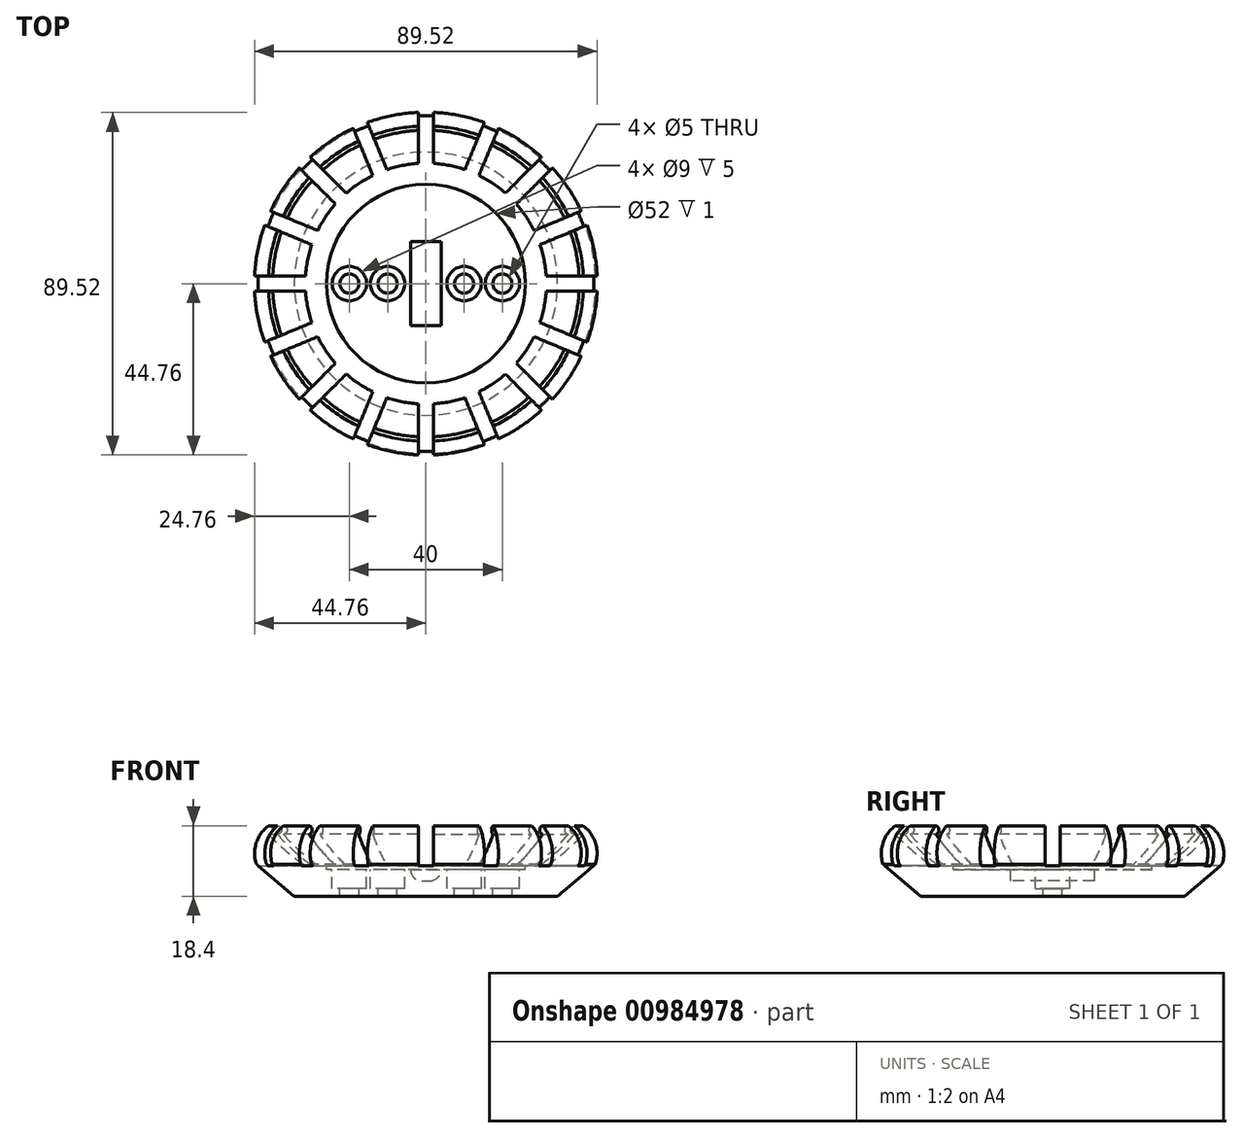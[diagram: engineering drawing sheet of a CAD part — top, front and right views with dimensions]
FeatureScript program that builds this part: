
annotation { "Feature Type Name" : "Feature", "Feature Type Description" : "" }
export const myFeature = defineFeature(function(context is Context, id is Id, definition is map)
    precondition{}
    {
        {
            var Q0;
            Q0=qCreatedBy(makeId("Front.planeOp"),FACE);
            var sketch = newSketch(context, id + "F0", { "sketchPlane" : qUnion([Q0])});
            skLineSegment(sketch, "E0", {"start": v(0, 0) * mm, "end": v(-31.5, 0) * mm});
            skArc(sketch, "E1", {"start": v(-41.2, 8.2) * mm, "mid": v(-36.58, 3.83) * mm, "end": v(-31.5, 0) * mm});
            skPoint(sketch, "E2.start.orphan", {"position": v(0, 8.2) * mm});
            skArc(sketch, "E3", {"start": v(-41.2, 8.2) * mm, "mid": v(-40.1, 9.3) * mm, "end": v(-41.2, 10.4) * mm});
            skLineSegment(sketch, "E4.trimOffspring", {"start": v(-41.2, 10.4) * mm, "end": v(-41.2, 14.25) * mm});
            skLineSegment(sketch, "E5", {"start": v(0, -8) * mm, "end": v(-34.43, -8) * mm});
            skLineSegment(sketch, "E6", {"start": v(-34.43, -8) * mm, "end": v(-44.37, 0.4) * mm});
            skArc(sketch, "E7", {"start": v(-41.2, 10.4) * mm, "mid": v(-44.4, 5.9) * mm, "end": v(-44.37, 0.4) * mm});
            skLineSegment(sketch, "E8.MirrorCS", {"start": v(0, 0) * mm, "end": v(31.5, 0) * mm});
            skArc(sketch, "E9.MirrorCS", {"start": v(41.2, 10.4) * mm, "mid": v(44.4, 5.9) * mm, "end": v(44.37, 0.4) * mm});
            skLineSegment(sketch, "E10.MirrorCS", {"start": v(41.2, 10.4) * mm, "end": v(41.2, 14.25) * mm});
            skLineSegment(sketch, "E11.MirrorCS", {"start": v(34.43, -8) * mm, "end": v(44.37, 0.4) * mm});
            skLineSegment(sketch, "E12.MirrorCS", {"start": v(0, -8) * mm, "end": v(34.43, -8) * mm});
            skArc(sketch, "E13.MirrorCS", {"start": v(41.2, 8.2) * mm, "mid": v(40.1, 9.3) * mm, "end": v(41.2, 10.4) * mm});
            skArc(sketch, "E14.MirrorCS", {"start": v(41.2, 8.2) * mm, "mid": v(36.58, 3.83) * mm, "end": v(31.5, 0) * mm});
            skLineSegment(sketch, "E15", {"start": v(0, 60.69) * mm, "end": v(0, -49.12) * mm});
            skSolve(sketch);
        }
        {
            var Q0;
            {var subQ1=sQuery(id+"F0.wireOp",EDGE,"E8.MirrorCS");Q0=makeQuery(id+"F0.imprint","IMPRINT",FACE,{"disambiguationData":[TD([[makeQuery(id+"F0.imprint","IMPRINT",EDGE,{"derivedFrom":subQ1}),-1.0]])]});}
            var Q1;
            Q1=sQuery(id+"F0.wireOp",EDGE,"E15");
            revolve(context, id + "F1", {"surfaceOperationType" : NewSurfaceOperationType.NEW, "entities" : qUnion([Q0]), "axis" : qUnion([Q1]), "revolveType" : RevolveType.FULL});
        }
        {
            var Q0;
            Q0=makeQuery(id+"F1.opRevolve","SWEPT_FACE",FACE,{"disambiguationData":[OSD([sQuery(id+"F0.wireOp",EDGE,"E8.MirrorCS")])]});
            var sketch = newSketch(context, id + "F2", { "sketchPlane" : qUnion([Q0])});
            skCircle(sketch, "E16", {"center": v(0, 0) * mm, "radius": 26 * mm});
            skSolve(sketch);
        }
        {
            var Q0;
            Q0 = qSketchRegion(id + "F2", true);
            extrude(context, id + "F3", {"entities" : qUnion([Q0]), "operationType" : NewBodyOperationType.REMOVE, "oppositeDirection" : true, "depth" : 1 * mm, "offsetDistance" : 25 * mm});
        }
        {
            var Q0;
            Q0=makeQuery(id+"F1.opRevolve","SWEPT_FACE",FACE,{"disambiguationData":[OSD([sQuery(id+"F0.wireOp",EDGE,"E8.MirrorCS")])]});
            var sketch = newSketch(context, id + "F4", { "sketchPlane" : qUnion([Q0])});
            skLineSegment(sketch, "E17.bottom", {"start": v(-2, 51.5) * mm, "end": v(2, 51.5) * mm});
            skLineSegment(sketch, "E17.top", {"start": v(-2, -48.5) * mm, "end": v(2, -48.5) * mm});
            skLineSegment(sketch, "E17.left", {"start": v(-2, 51.5) * mm, "end": v(-2, 4.83) * mm});
            skLineSegment(sketch, "E17.right", {"start": v(2, 51.5) * mm, "end": v(2, 4.83) * mm});
            skLineSegment(sketch, "E18.bottom", {"start": v(-48.8, 2) * mm, "end": v(-4.83, 2) * mm});
            skLineSegment(sketch, "E18.top", {"start": v(-48.8, -2) * mm, "end": v(-4.83, -2) * mm});
            skLineSegment(sketch, "E18.left", {"start": v(-48.8, 2) * mm, "end": v(-48.8, -2) * mm});
            skLineSegment(sketch, "E18.right", {"start": v(51.2, 2) * mm, "end": v(51.2, -2) * mm});
            skLineSegment(sketch, "E19", {"start": v(-36.98, 39.81) * mm, "end": v(-2, 4.83) * mm});
            skLineSegment(sketch, "E20", {"start": v(38.72, -35.9) * mm, "end": v(35.9, -38.72) * mm});
            skLineSegment(sketch, "E21", {"start": v(35.9, -38.72) * mm, "end": v(2, -4.83) * mm});
            skLineSegment(sketch, "E22", {"start": v(-39.72, 36.89) * mm, "end": v(-36.98, 39.81) * mm});
            skLineSegment(sketch, "E23", {"start": v(44.09, 41.26) * mm, "end": v(4.83, 2) * mm});
            skLineSegment(sketch, "E24", {"start": v(-37.99, -40.82) * mm, "end": v(-40.82, -37.99) * mm});
            skLineSegment(sketch, "E25", {"start": v(-40.82, -37.99) * mm, "end": v(-4.83, -2) * mm});
            skLineSegment(sketch, "E26", {"start": v(41.17, 44) * mm, "end": v(44.09, 41.26) * mm});
            skLineSegment(sketch, "E27.trimOffspring", {"start": v(-4.83, 2) * mm, "end": v(-39.72, 36.89) * mm});
            skLineSegment(sketch, "E28.trimOffspring", {"start": v(2, 4.83) * mm, "end": v(41.17, 44) * mm});
            skLineSegment(sketch, "E29.trimOffspring", {"start": v(4.83, 2) * mm, "end": v(51.2, 2) * mm});
            skLineSegment(sketch, "E30.trimOffspring", {"start": v(4.83, -2) * mm, "end": v(38.72, -35.9) * mm});
            skLineSegment(sketch, "E31.trimOffspring", {"start": v(4.83, -2) * mm, "end": v(51.2, -2) * mm});
            skLineSegment(sketch, "E32.trimOffspring", {"start": v(2, -4.83) * mm, "end": v(2, -48.5) * mm});
            skLineSegment(sketch, "E33.trimOffspring", {"start": v(-2, -4.83) * mm, "end": v(-37.99, -40.82) * mm});
            skLineSegment(sketch, "E34.trimOffspring", {"start": v(-2, -4.83) * mm, "end": v(-2, -48.5) * mm});
            skLineSegment(sketch, "E35", {"start": v(0, 0) * mm, "end": v(-2, 4.83) * mm});
            skLineSegment(sketch, "E36", {"start": v(0, 0) * mm, "end": v(-4.83, 2) * mm});
            skLineSegment(sketch, "E37", {"start": v(-22.85, 49.94) * mm, "end": v(21.03, -56) * mm});
            skLineSegment(sketch, "E38", {"start": v(21.03, -56) * mm, "end": v(24.73, -54.47) * mm});
            skLineSegment(sketch, "E39", {"start": v(24.73, -54.47) * mm, "end": v(-19.15, 51.46) * mm});
            skLineSegment(sketch, "E40", {"start": v(-50.13, 22.93) * mm, "end": v(51.7, -19.25) * mm});
            skLineSegment(sketch, "E41", {"start": v(51.7, -19.25) * mm, "end": v(50.17, -22.95) * mm});
            skLineSegment(sketch, "E42", {"start": v(50.17, -22.95) * mm, "end": v(-51.66, 19.23) * mm});
            skLineSegment(sketch, "E43", {"start": v(0, 0) * mm, "end": v(20.45, 49.36) * mm});
            skLineSegment(sketch, "E44", {"start": v(0, 0) * mm, "end": v(52.24, 21.64) * mm});
            skLineSegment(sketch, "E45", {"start": v(-50.13, 22.93) * mm, "end": v(-51.66, 19.23) * mm});
            skLineSegment(sketch, "E46", {"start": v(-22.85, 49.94) * mm, "end": v(-19.15, 51.46) * mm});
            skLineSegment(sketch, "E47", {"start": v(53.21, 19.88) * mm, "end": v(-45.17, -20.88) * mm});
            skLineSegment(sketch, "E48", {"start": v(-45.17, -20.88) * mm, "end": v(-46.7, -17.18) * mm});
            skLineSegment(sketch, "E49", {"start": v(-46.7, -17.18) * mm, "end": v(52.6, 23.95) * mm});
            skLineSegment(sketch, "E50", {"start": v(52.6, 23.95) * mm, "end": v(53.21, 19.88) * mm});
            skLineSegment(sketch, "E51", {"start": v(22.61, 49.36) * mm, "end": v(-17.93, -48.5) * mm});
            skLineSegment(sketch, "E52", {"start": v(-17.93, -48.5) * mm, "end": v(-21.62, -46.97) * mm});
            skLineSegment(sketch, "E53", {"start": v(-21.62, -46.97) * mm, "end": v(18.47, 49.81) * mm});
            skLineSegment(sketch, "E54", {"start": v(18.47, 49.81) * mm, "end": v(22.61, 48.1) * mm});
            skSolve(sketch);
        }
        {
            var Q0;
            Q0 = qSketchRegion(id + "F4", true);
            extrude(context, id + "F5", {"entities" : qUnion([Q0]), "operationType" : NewBodyOperationType.REMOVE, "depth" : 25 * mm, "offsetDistance" : 25 * mm});
        }
        {
            var Q0;
            {var subQ0=sQuery(id+"F0.wireOp",EDGE,"E9.MirrorCS");var subQ1=sQuery(id+"F0.wireOp",EDGE,"E11.MirrorCS");Q0=makeQuery(id+"F5.boolean.opBoolean","SPLIT",EDGE,{"disambiguationData":[TD([makeQuery(id+"F5.opExtrude","SWEPT_FACE",FACE,{"disambiguationData":[OSD([sQuery(id+"F4.wireOp",EDGE,"E17.left")])]})])],"derivedFrom":makeQuery(id+"F1.opRevolve","SWEPT_EDGE",EDGE,{"disambiguationData":[OSD([subQ0,subQ1])]})});}
            var Q1;
            {var subQ0=sQuery(id+"F0.wireOp",EDGE,"E9.MirrorCS");var subQ1=sQuery(id+"F0.wireOp",EDGE,"E11.MirrorCS");Q1=makeQuery(id+"F5.boolean.opBoolean","SPLIT",EDGE,{"disambiguationData":[TD([makeQuery(id+"F5.opExtrude","SWEPT_FACE",FACE,{"disambiguationData":[OSD([sQuery(id+"F4.wireOp",EDGE,"E17.right")])]})])],"derivedFrom":makeQuery(id+"F1.opRevolve","SWEPT_EDGE",EDGE,{"disambiguationData":[OSD([subQ0,subQ1])]})});}
            var Q2;
            {var subQ0=sQuery(id+"F0.wireOp",EDGE,"E9.MirrorCS");var subQ1=sQuery(id+"F0.wireOp",EDGE,"E11.MirrorCS");Q2=makeQuery(id+"F5.boolean.opBoolean","SPLIT",EDGE,{"disambiguationData":[TD([makeQuery(id+"F5.opExtrude","SWEPT_FACE",FACE,{"disambiguationData":[OSD([sQuery(id+"F4.wireOp",EDGE,"E23")])]})])],"derivedFrom":makeQuery(id+"F1.opRevolve","SWEPT_EDGE",EDGE,{"disambiguationData":[OSD([subQ0,subQ1])]})});}
            var Q3;
            {var subQ0=sQuery(id+"F0.wireOp",EDGE,"E9.MirrorCS");var subQ1=sQuery(id+"F0.wireOp",EDGE,"E11.MirrorCS");Q3=makeQuery(id+"F5.boolean.opBoolean","SPLIT",EDGE,{"disambiguationData":[TD([makeQuery(id+"F5.opExtrude","SWEPT_FACE",FACE,{"disambiguationData":[OSD([sQuery(id+"F4.wireOp",EDGE,"E30.trimOffspring")])]})])],"derivedFrom":makeQuery(id+"F1.opRevolve","SWEPT_EDGE",EDGE,{"disambiguationData":[OSD([subQ0,subQ1])]})});}
            var Q4;
            {var subQ0=sQuery(id+"F0.wireOp",EDGE,"E9.MirrorCS");var subQ1=sQuery(id+"F0.wireOp",EDGE,"E11.MirrorCS");Q4=makeQuery(id+"F5.boolean.opBoolean","SPLIT",EDGE,{"disambiguationData":[TD([makeQuery(id+"F5.opExtrude","SWEPT_FACE",FACE,{"disambiguationData":[OSD([sQuery(id+"F4.wireOp",EDGE,"E21")])]})])],"derivedFrom":makeQuery(id+"F1.opRevolve","SWEPT_EDGE",EDGE,{"disambiguationData":[OSD([subQ0,subQ1])]})});}
            var Q5;
            {var subQ0=sQuery(id+"F0.wireOp",EDGE,"E9.MirrorCS");var subQ1=sQuery(id+"F0.wireOp",EDGE,"E11.MirrorCS");Q5=makeQuery(id+"F5.boolean.opBoolean","SPLIT",EDGE,{"disambiguationData":[TD([makeQuery(id+"F5.opExtrude","SWEPT_FACE",FACE,{"disambiguationData":[OSD([sQuery(id+"F4.wireOp",EDGE,"E33.trimOffspring")])]})])],"derivedFrom":makeQuery(id+"F1.opRevolve","SWEPT_EDGE",EDGE,{"disambiguationData":[OSD([subQ0,subQ1])]})});}
            var Q6;
            {var subQ0=sQuery(id+"F0.wireOp",EDGE,"E9.MirrorCS");var subQ1=sQuery(id+"F0.wireOp",EDGE,"E11.MirrorCS");Q6=makeQuery(id+"F5.boolean.opBoolean","SPLIT",EDGE,{"disambiguationData":[TD([makeQuery(id+"F5.opExtrude","SWEPT_FACE",FACE,{"disambiguationData":[OSD([sQuery(id+"F4.wireOp",EDGE,"E18.top")])]})])],"derivedFrom":makeQuery(id+"F1.opRevolve","SWEPT_EDGE",EDGE,{"disambiguationData":[OSD([subQ0,subQ1])]})});}
            var Q7;
            {var subQ0=sQuery(id+"F0.wireOp",EDGE,"E9.MirrorCS");var subQ1=sQuery(id+"F0.wireOp",EDGE,"E11.MirrorCS");Q7=makeQuery(id+"F5.boolean.opBoolean","SPLIT",EDGE,{"disambiguationData":[TD([makeQuery(id+"F5.opExtrude","SWEPT_FACE",FACE,{"disambiguationData":[OSD([sQuery(id+"F4.wireOp",EDGE,"E18.bottom")])]})])],"derivedFrom":makeQuery(id+"F1.opRevolve","SWEPT_EDGE",EDGE,{"disambiguationData":[OSD([subQ0,subQ1])]})});}
            fillet(context, id + "F6", {"entities" : qUnion([Q0, Q1, Q2, Q3, Q4, Q5, Q6, Q7]), "radius" : 2 * mm, "tangentPropagation" : true, "allowEdgeOverflow" : false});
        }
        {
            var Q0;
            Q0=makeQuery(id+"F3.boolean.opBoolean","COPY",FACE,{"derivedFrom":makeQuery(id+"F3.opExtrude","CAP_FACE",FACE,{"disambiguationData":[OSD([sQuery(id+"F2.wireOp",EDGE,"E16")])],"isStart":false})});
            var sketch = newSketch(context, id + "F7", { "sketchPlane" : qUnion([Q0])});
            skPoint(sketch, "E55", {"position": v(-20, 0) * mm});
            skPoint(sketch, "E56", {"position": v(-10, 0) * mm});
            skPoint(sketch, "E57", {"position": v(10, 0) * mm});
            skPoint(sketch, "E58", {"position": v(20, 0) * mm});
            skSolve(sketch);
        }
        {
            var Q0;
            Q0=sQuery(id+"F7.wireOp",VERTEX,"E58");
            var Q1;
            Q1=sQuery(id+"F7.wireOp",VERTEX,"E57");
            var Q2;
            Q2=sQuery(id+"F7.wireOp",VERTEX,"E56");
            var Q3;
            Q3=sQuery(id+"F7.wireOp",VERTEX,"E55");
            var Q4;
            Q4=makeQuery(id+"F1.opRevolve","SWEPT_BODY",BODY,{"disambiguationData":[OSD([sQuery(id+"F0.wireOp",EDGE,"E8.MirrorCS"),sQuery(id+"F0.wireOp",EDGE,"E9.MirrorCS"),sQuery(id+"F0.wireOp",EDGE,"E11.MirrorCS"),sQuery(id+"F0.wireOp",EDGE,"E12.MirrorCS"),sQuery(id+"F0.wireOp",EDGE,"E13.MirrorCS"),sQuery(id+"F0.wireOp",EDGE,"E14.MirrorCS"),sQuery(id+"F0.wireOp",EDGE,"E15")])]});
            hole(context, id + "F8", {"style" : HoleStyle.C_BORE, "endStyle" : HoleEndStyle.BLIND, "holeDiameter" : 5 * mm, "cBoreDiameter" : 9 * mm, "cBoreDepth" : 5 * mm, "majorDiameter" : 5 * mm, "holeDepth" : 8 * mm, "isTappedThrough" : true, "tappedDepth" : 12 * mm, "tapClearance" : 3, "startFromSketch" : true, "locations" : qUnion([Q0, Q1, Q2, Q3]), "scope" : qUnion([Q4])});
        }
        {
            var Q0;
            Q0=makeQuery(id+"F3.boolean.opBoolean","COPY",FACE,{"derivedFrom":makeQuery(id+"F3.opExtrude","CAP_FACE",FACE,{"disambiguationData":[OSD([sQuery(id+"F2.wireOp",EDGE,"E16")])],"isStart":false})});
            var sketch = newSketch(context, id + "F9", { "sketchPlane" : qUnion([Q0])});
            skLineSegment(sketch, "E59.bottom", {"start": v(-4, 11) * mm, "end": v(4, 11) * mm});
            skLineSegment(sketch, "E59.top", {"start": v(-4, -11) * mm, "end": v(4, -11) * mm});
            skLineSegment(sketch, "E59.left", {"start": v(-4, 11) * mm, "end": v(-4, -11) * mm});
            skLineSegment(sketch, "E59.right", {"start": v(4, 11) * mm, "end": v(4, -11) * mm});
            skSolve(sketch);
        }
        {
            var Q0;
            Q0=makeQuery(id+"F9.imprint","IMPRINT",FACE,{"disambiguationData":[TD([[makeQuery(id+"F9.imprint","IMPRINT",EDGE,{"derivedFrom":sQuery(id+"F9.wireOp",EDGE,"E59.bottom")}),-1.0]])]});
            var sketch = newSketch(context, id + "F10", { "sketchPlane" : qUnion([Q0])});
            skSolve(sketch);
        }
        {
            var Q0;
            Q0 = qSketchRegion(id + "F10", true);
            var Q1;
            Q1=makeQuery(id+"F10.imprint","IMPRINT",FACE,{"disambiguationData":[TD([[makeQuery(id+"F10.imprint","IMPRINT",EDGE,{"derivedFrom":makeQuery(id+"F9.imprint","IMPRINT",EDGE,{"derivedFrom":sQuery(id+"F9.wireOp",EDGE,"E59.bottom")})}),-1.0]])]});
            extrude(context, id + "F11", {"entities" : qUnion([Q0, Q1]), "operationType" : NewBodyOperationType.REMOVE, "oppositeDirection" : true, "depth" : 3 * mm, "offsetDistance" : 25 * mm});
        }
        {
            var Q0;
            Q0=makeQuery(id+"F11.boolean.opBoolean","COPY",EDGE,{"derivedFrom":makeQuery(id+"F11.opExtrude","CAP_EDGE",EDGE,{"disambiguationData":[OSD([sQuery(id+"F9.wireOp",EDGE,"E59.left")])],"isStart":false})});
            var Q1;
            Q1=makeQuery(id+"F11.boolean.opBoolean","COPY",EDGE,{"derivedFrom":makeQuery(id+"F11.opExtrude","CAP_EDGE",EDGE,{"disambiguationData":[OSD([sQuery(id+"F9.wireOp",EDGE,"E59.right")])],"isStart":false})});
            fillet(context, id + "F12", {"entities" : qUnion([Q0, Q1]), "radius" : 3 * mm, "tangentPropagation" : true, "allowEdgeOverflow" : false});
        }
    });
